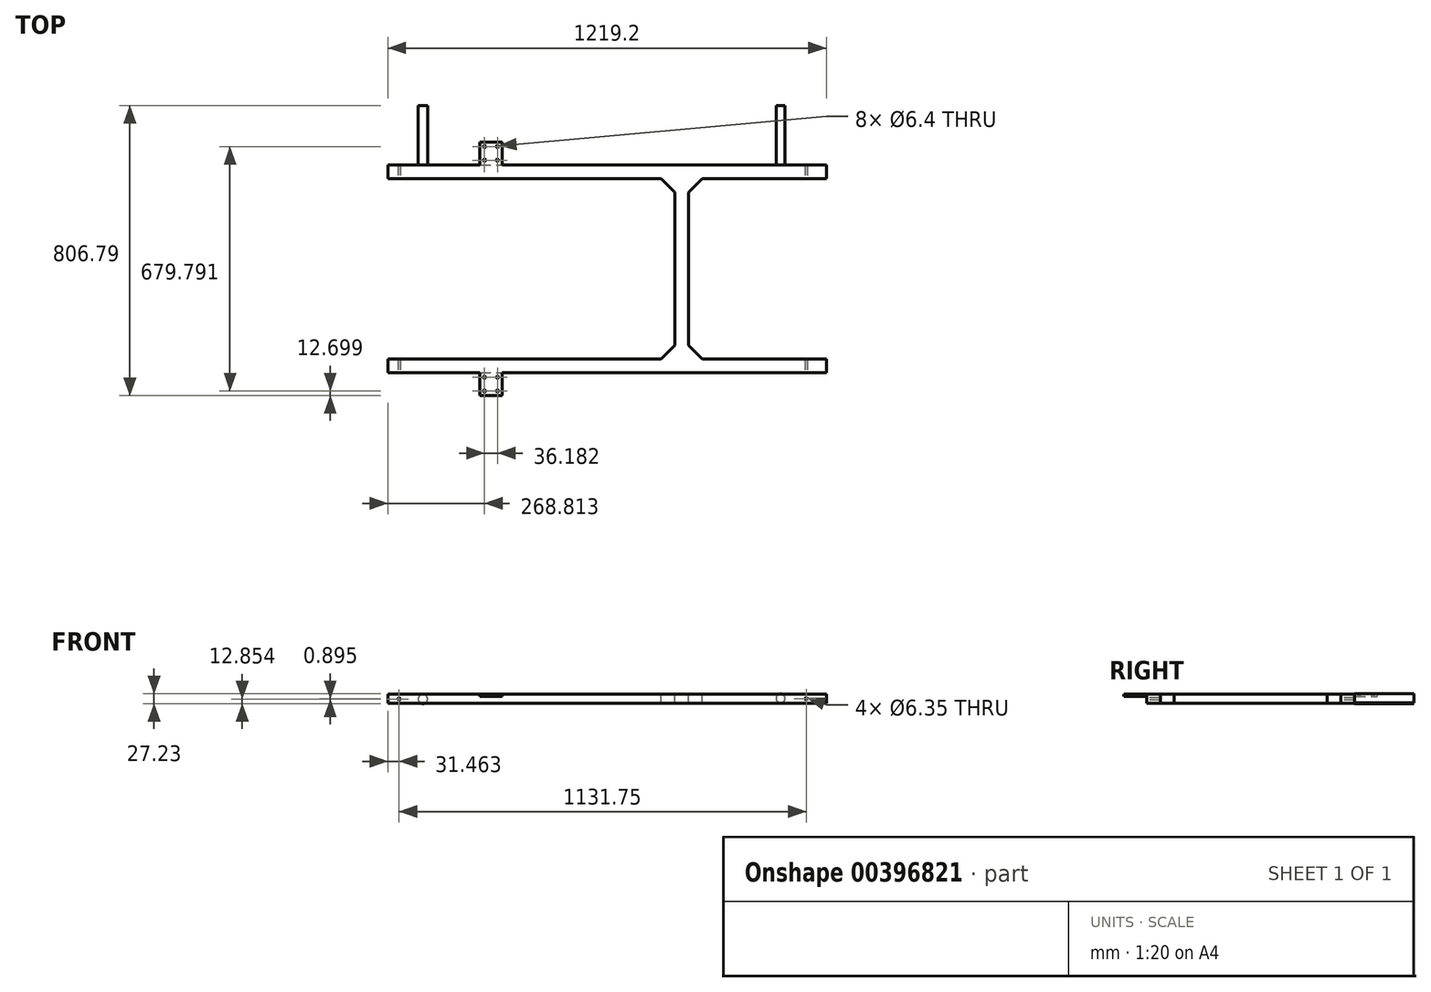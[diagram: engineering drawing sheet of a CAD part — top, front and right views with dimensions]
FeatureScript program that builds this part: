
annotation { "Feature Type Name" : "Feature", "Feature Type Description" : "" }
export const myFeature = defineFeature(function(context is Context, id is Id, definition is map)
    precondition{}
    {
        {
            var Q0;
            Q0=qCreatedBy(makeId("Top.planeOp"),FACE);
            var sketch = newSketch(context, id + "F0", { "sketchPlane" : qUnion([Q0])});
            skLineSegment(sketch, "E0", {"start": v(-609.6, 0) * mm, "end": v(609.6, 0) * mm});
            skLineSegment(sketch, "E1", {"start": v(-609.6, 0) * mm, "end": v(-609.6, -38.1) * mm});
            skLineSegment(sketch, "E2", {"start": v(-609.6, -38.1) * mm, "end": v(609.6, -38.1) * mm});
            skLineSegment(sketch, "E3", {"start": v(609.6, -38.1) * mm, "end": v(609.6, 0) * mm});
            skLineSegment(sketch, "E4", {"start": v(226.94, -38.1) * mm, "end": v(226.94, -540.1) * mm});
            skLineSegment(sketch, "E5", {"start": v(609.6, -540.1) * mm, "end": v(-609.6, -540.1) * mm});
            skLineSegment(sketch, "E6", {"start": v(-609.6, -540.1) * mm, "end": v(-609.6, -578.2) * mm});
            skLineSegment(sketch, "E7", {"start": v(-609.6, -578.2) * mm, "end": v(609.6, -578.2) * mm});
            skLineSegment(sketch, "E8", {"start": v(609.6, -578.2) * mm, "end": v(609.6, -540.1) * mm});
            skLineSegment(sketch, "E9", {"start": v(188.84, -38.1) * mm, "end": v(188.84, -540.1) * mm});
            skLineSegment(sketch, "E10", {"start": v(150.74, -540.1) * mm, "end": v(188.84, -502) * mm});
            skLineSegment(sketch, "E11", {"start": v(226.94, -502) * mm, "end": v(265.04, -540.1) * mm});
            skLineSegment(sketch, "E12", {"start": v(188.84, -76.2) * mm, "end": v(150.74, -38.1) * mm});
            skLineSegment(sketch, "E13", {"start": v(226.94, -76.2) * mm, "end": v(265.04, -38.1) * mm});
            skLineSegment(sketch, "E14", {"start": v(-353.49, -578.2) * mm, "end": v(-353.49, -641.7) * mm});
            skLineSegment(sketch, "E15", {"start": v(-353.49, -641.7) * mm, "end": v(-291.9, -641.7) * mm});
            skLineSegment(sketch, "E16", {"start": v(-291.9, -641.7) * mm, "end": v(-291.9, -578.2) * mm});
            skLineSegment(sketch, "E17", {"start": v(-353.49, 0) * mm, "end": v(-353.49, 63.5) * mm});
            skLineSegment(sketch, "E18", {"start": v(-353.49, 63.5) * mm, "end": v(-291.9, 63.5) * mm});
            skLineSegment(sketch, "E19", {"start": v(-291.9, 63.5) * mm, "end": v(-291.9, 0) * mm});
            skCircle(sketch, "E20", {"center": v(-340.79, 50.8) * mm, "radius": 3.2 * mm});
            skCircle(sketch, "E21", {"center": v(-340.79, 12.7) * mm, "radius": 3.2 * mm});
            skCircle(sketch, "E22", {"center": v(-304.6, 12.7) * mm, "radius": 3.2 * mm});
            skCircle(sketch, "E23", {"center": v(-304.6, 50.8) * mm, "radius": 3.2 * mm});
            skCircle(sketch, "E24", {"center": v(-340.79, -590.9) * mm, "radius": 3.2 * mm});
            skCircle(sketch, "E25", {"center": v(-304.6, -590.9) * mm, "radius": 3.2 * mm});
            skCircle(sketch, "E26", {"center": v(-304.6, -629) * mm, "radius": 3.2 * mm});
            skCircle(sketch, "E27", {"center": v(-340.79, -629) * mm, "radius": 3.2 * mm});
            skSolve(sketch);
        }
        {
            var Q0;
            {var subQ0=sQuery(id+"F0.wireOp",EDGE,"E1");Q0=makeQuery(id+"F0.imprint","IMPRINT",FACE,{"disambiguationData":[TD([[makeQuery(id+"F0.imprint","IMPRINT",EDGE,{"derivedFrom":subQ0}),1.0]])]});}
            var Q1;
            {var subQ5=sQuery(id+"F0.wireOp",EDGE,"E6");Q1=makeQuery(id+"F0.imprint","IMPRINT",FACE,{"disambiguationData":[TD([[makeQuery(id+"F0.imprint","IMPRINT",EDGE,{"derivedFrom":subQ5}),1.0]])]});}
            var Q2;
            {var subQ3=sQuery(id+"F0.wireOp",EDGE,"E10");Q2=makeQuery(id+"F0.imprint","IMPRINT",FACE,{"disambiguationData":[TD([[makeQuery(id+"F0.imprint","IMPRINT",EDGE,{"derivedFrom":subQ3}),-1.0]])]});}
            var Q3;
            {var subQ3=sQuery(id+"F0.wireOp",EDGE,"E11");Q3=makeQuery(id+"F0.imprint","IMPRINT",FACE,{"disambiguationData":[TD([[makeQuery(id+"F0.imprint","IMPRINT",EDGE,{"derivedFrom":subQ3}),-1.0]])]});}
            var Q4;
            {var subQ1=sQuery(id+"F0.wireOp",EDGE,"E4");var subQ5=sQuery(id+"F0.wireOp",EDGE,"E2");var subQ6=makeQuery(id+"F0.imprint","INTERSECT",VERTEX,{"derivedFrom":[subQ5,subQ1]});Q4=makeQuery(id+"F0.imprint","IMPRINT",FACE,{"disambiguationData":[TD([[makeQuery(id+"F0.imprint","IMPRINT",EDGE,{"disambiguationData":[TD([[subQ6,1.0]])],"derivedFrom":subQ5}),-1.0]])]});}
            var Q5;
            {var subQ3=sQuery(id+"F0.wireOp",EDGE,"E12");Q5=makeQuery(id+"F0.imprint","IMPRINT",FACE,{"disambiguationData":[TD([[makeQuery(id+"F0.imprint","IMPRINT",EDGE,{"derivedFrom":subQ3}),-1.0]])]});}
            var Q6;
            {var subQ3=sQuery(id+"F0.wireOp",EDGE,"E13");Q6=makeQuery(id+"F0.imprint","IMPRINT",FACE,{"disambiguationData":[TD([[makeQuery(id+"F0.imprint","IMPRINT",EDGE,{"derivedFrom":subQ3}),1.0]])]});}
            extrude(context, id + "F1", {"entities" : qUnion([Q0, Q1, Q2, Q3, Q4, Q5, Q6]), "oppositeDirection" : true, "depth" : 25.4 * mm});
        }
        {
            var Q0;
            {var subQ0=sQuery(id+"F0.wireOp",EDGE,"E14");Q0=makeQuery(id+"F0.imprint","IMPRINT",FACE,{"disambiguationData":[TD([[makeQuery(id+"F0.imprint","IMPRINT",EDGE,{"derivedFrom":subQ0}),1.0]])]});}
            var Q1;
            {var subQ0=sQuery(id+"F0.wireOp",EDGE,"E17");Q1=makeQuery(id+"F0.imprint","IMPRINT",FACE,{"disambiguationData":[TD([[makeQuery(id+"F0.imprint","IMPRINT",EDGE,{"derivedFrom":subQ0}),-1.0]])]});}
            extrude(context, id + "F2", {"entities" : qUnion([Q0, Q1]), "operationType" : NewBodyOperationType.ADD, "oppositeDirection" : true, "depth" : 6.35 * mm});
        }
        {
            var Q0;
            Q0=makeQuery(id+"F1.opExtrude","SWEPT_FACE",FACE,{"disambiguationData":[OSD([sQuery(id+"F0.wireOp",EDGE,"E7")])]});
            var sketch = newSketch(context, id + "F3", { "sketchPlane" : qUnion([Q0])});
            skCircle(sketch, "E28", {"center": v(-578.14, -13.22) * mm, "radius": 6.87 * mm});
            skCircle(sketch, "E29", {"center": v(553.62, -12.32) * mm, "radius": 6.87 * mm});
            skSolve(sketch);
        }
        {
            var Q0;
            Q0=sQuery(id+"F3.wireOp",VERTEX,"E28.center");
            var Q1;
            Q1=makeQuery(id+"F1.opExtrude","SWEPT_BODY",BODY,{"disambiguationData":[OSD([sQuery(id+"F0.wireOp",EDGE,"E0"),sQuery(id+"F0.wireOp",EDGE,"E1"),sQuery(id+"F0.wireOp",EDGE,"E2"),sQuery(id+"F0.wireOp",EDGE,"E3"),sQuery(id+"F0.wireOp",EDGE,"E4"),sQuery(id+"F0.wireOp",EDGE,"E5"),sQuery(id+"F0.wireOp",EDGE,"E6"),sQuery(id+"F0.wireOp",EDGE,"E7"),sQuery(id+"F0.wireOp",EDGE,"E8"),sQuery(id+"F0.wireOp",EDGE,"E9"),sQuery(id+"F0.wireOp",EDGE,"E10"),sQuery(id+"F0.wireOp",EDGE,"E11"),sQuery(id+"F0.wireOp",EDGE,"E12"),sQuery(id+"F0.wireOp",EDGE,"E13")])]});
            hole(context, id + "F4", {"style" : HoleStyle.SIMPLE, "endStyle" : HoleEndStyle.THROUGH, "holeDiameter" : 6.35 * mm, "startFromSketch" : true, "locations" : qUnion([Q0]), "scope" : qUnion([Q1]), "isTappedThrough" : true});
        }
        {
            var Q0;
            Q0=sQuery(id+"F3.wireOp",VERTEX,"E29.center");
            var Q1;
            Q1=makeQuery(id+"F1.opExtrude","SWEPT_BODY",BODY,{"disambiguationData":[OSD([sQuery(id+"F0.wireOp",EDGE,"E0"),sQuery(id+"F0.wireOp",EDGE,"E1"),sQuery(id+"F0.wireOp",EDGE,"E2"),sQuery(id+"F0.wireOp",EDGE,"E3"),sQuery(id+"F0.wireOp",EDGE,"E4"),sQuery(id+"F0.wireOp",EDGE,"E5"),sQuery(id+"F0.wireOp",EDGE,"E6"),sQuery(id+"F0.wireOp",EDGE,"E7"),sQuery(id+"F0.wireOp",EDGE,"E8"),sQuery(id+"F0.wireOp",EDGE,"E9"),sQuery(id+"F0.wireOp",EDGE,"E10"),sQuery(id+"F0.wireOp",EDGE,"E11"),sQuery(id+"F0.wireOp",EDGE,"E12"),sQuery(id+"F0.wireOp",EDGE,"E13")])]});
            hole(context, id + "F5", {"style" : HoleStyle.SIMPLE, "endStyle" : HoleEndStyle.THROUGH, "holeDiameter" : 6.35 * mm, "startFromSketch" : true, "locations" : qUnion([Q0]), "scope" : qUnion([Q1]), "isTappedThrough" : true});
        }
        {
            var Q0;
            Q0=qCreatedBy(makeId("Front.planeOp"),FACE);
            var sketch = newSketch(context, id + "F6", { "sketchPlane" : qUnion([Q0])});
            skCircle(sketch, "E30", {"center": v(482.4, -11.35) * mm, "radius": 12.5 * mm});
            skSolve(sketch);
        }
        {
            var Q0;
            Q0=makeQuery(id+"F6.imprint","IMPRINT",FACE,{"disambiguationData":[TD([[makeQuery(id+"F6.imprint","IMPRINT",EDGE,{"derivedFrom":sQuery(id+"F6.wireOp",EDGE,"E30")}),1.0]])]});
            extrude(context, id + "F7", {"entities" : qUnion([Q0]), "oppositeDirection" : true, "depth" : 165.1 * mm});
        }
        {
            var Q0;
            Q0=qCreatedBy(makeId("Front.planeOp"),FACE);
            var sketch = newSketch(context, id + "F8", { "sketchPlane" : qUnion([Q0])});
            skCircle(sketch, "E31", {"center": v(-512, -13.13) * mm, "radius": 12.94 * mm});
            skSolve(sketch);
        }
        {
            var Q0;
            Q0=makeQuery(id+"F8.imprint","IMPRINT",FACE,{"disambiguationData":[TD([[makeQuery(id+"F8.imprint","IMPRINT",EDGE,{"derivedFrom":sQuery(id+"F8.wireOp",EDGE,"E31")}),1.0]])]});
            extrude(context, id + "F9", {"entities" : qUnion([Q0]), "oppositeDirection" : true, "depth" : 165.1 * mm});
        }
    });
